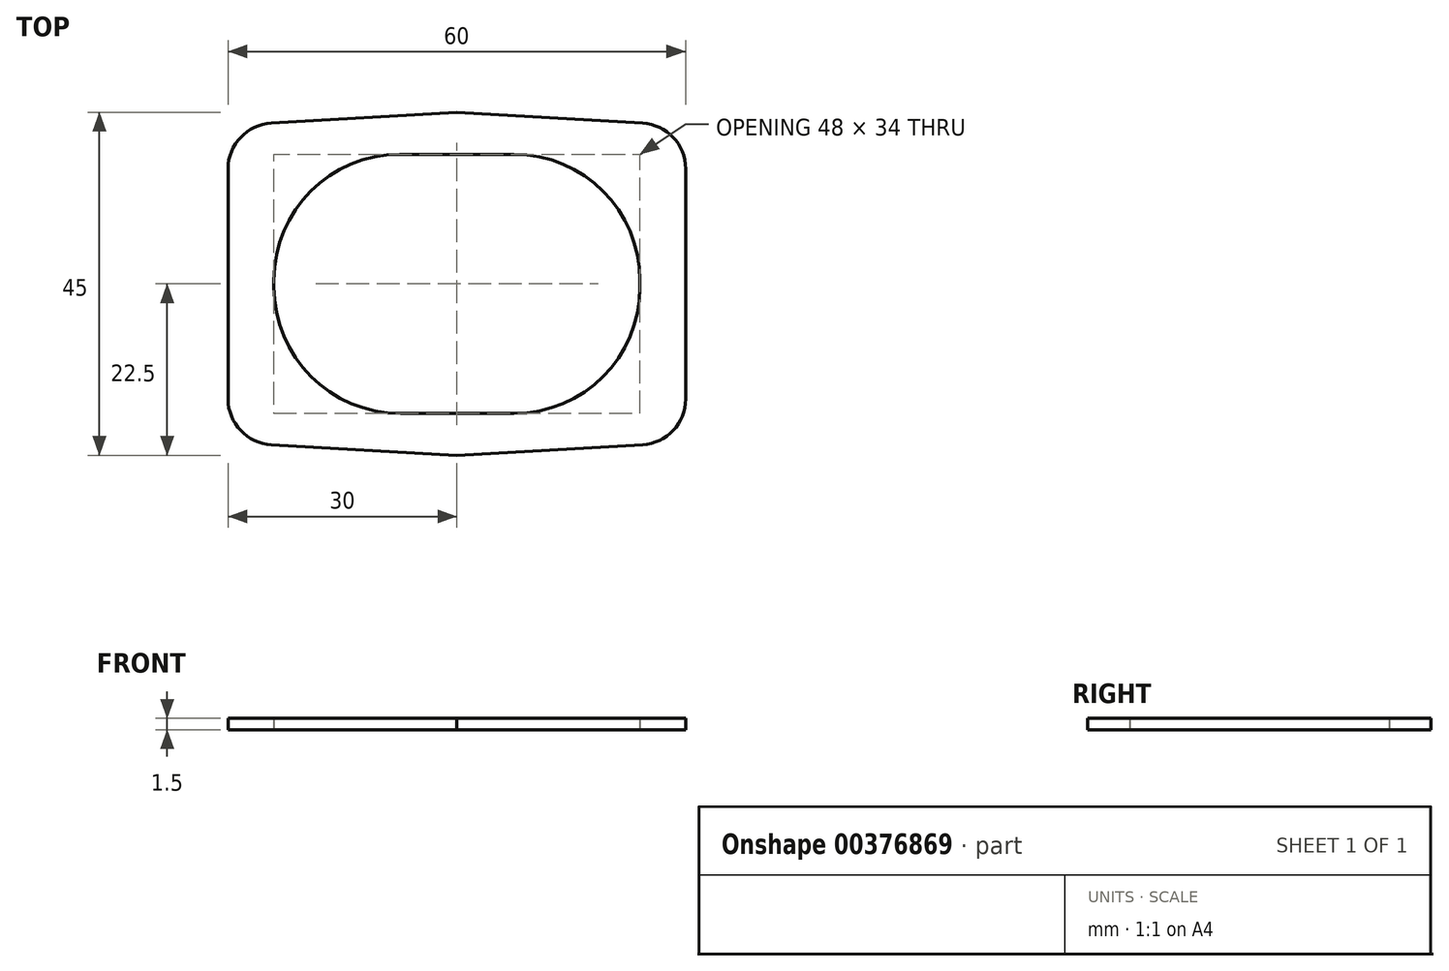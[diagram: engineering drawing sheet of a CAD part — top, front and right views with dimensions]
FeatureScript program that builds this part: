
annotation { "Feature Type Name" : "Feature", "Feature Type Description" : "" }
export const myFeature = defineFeature(function(context is Context, id is Id, definition is map)
    precondition{}
    {
        {
            var Q0;
            Q0=qCreatedBy(makeId("Top.planeOp"),FACE);
            var sketch = newSketch(context, id + "F0", { "sketchPlane" : qUnion([Q0])});
            skLineSegment(sketch, "E0.bottom", {"start": v(7.5, -17) * mm, "end": v(-7.4, -17) * mm});
            skLineSegment(sketch, "E0.top", {"start": v(7.5, 17) * mm, "end": v(-7.5, 17) * mm});
            skLineSegment(sketch, "E0.left", {"start": v(24, -0.5) * mm, "end": v(24, 0.5) * mm});
            skLineSegment(sketch, "E0.right", {"start": v(-24, -0.4) * mm, "end": v(-24, 0.5) * mm});
            skPoint(sketch, "E0.middle", {"position": v(0, 0) * mm});
            skPoint(sketch, "E1.visualSharp", {"position": v(-24, 17) * mm});
            skArc(sketch, "E1.filletArc", {"start": v(-7.5, 17) * mm, "mid": v(-19.17, 12.17) * mm, "end": v(-24, 0.5) * mm});
            skPoint(sketch, "E2.visualSharp", {"position": v(24, 17) * mm});
            skArc(sketch, "E2.filletArc", {"start": v(24, 0.5) * mm, "mid": v(19.17, 12.17) * mm, "end": v(7.5, 17) * mm});
            skPoint(sketch, "E3.visualSharp", {"position": v(24, -17) * mm});
            skArc(sketch, "E3.filletArc", {"start": v(7.5, -17) * mm, "mid": v(19.17, -12.17) * mm, "end": v(24, -0.5) * mm});
            skPoint(sketch, "E4.visualSharp", {"position": v(-24, -17) * mm});
            skArc(sketch, "E4.filletArc", {"start": v(-24, -0.4) * mm, "mid": v(-19.14, -12.14) * mm, "end": v(-7.4, -17) * mm});
            skLineSegment(sketch, "E5.left", {"start": v(30, -15.1) * mm, "end": v(30, 15.1) * mm});
            skLineSegment(sketch, "E5.right", {"start": v(-30, -15.1) * mm, "end": v(-30, 15.1) * mm});
            skPoint(sketch, "E6.visualSharp", {"position": v(-30, 22.5) * mm});
            skPoint(sketch, "E7.visualSharp", {"position": v(30, 22.5) * mm});
            skPoint(sketch, "E8.visualSharp", {"position": v(30, -22.5) * mm});
            skPoint(sketch, "E9.visualSharp", {"position": v(-30, -22.5) * mm});
            skPoint(sketch, "E10", {"position": v(0, 22.5) * mm});
            skPoint(sketch, "E11", {"position": v(0, -22.5) * mm});
            skLineSegment(sketch, "E12", {"start": v(0, 22.5) * mm, "end": v(-24.35, 21.1) * mm});
            skLineSegment(sketch, "E13", {"start": v(0, 22.5) * mm, "end": v(24.35, 21.1) * mm});
            skLineSegment(sketch, "E14", {"start": v(0, -22.5) * mm, "end": v(24.35, -21.1) * mm});
            skLineSegment(sketch, "E15", {"start": v(0, -22.5) * mm, "end": v(-24.35, -21.1) * mm});
            skArc(sketch, "E16.filletArc", {"start": v(-24.35, 21.1) * mm, "mid": v(-28.36, 19.22) * mm, "end": v(-30, 15.1) * mm});
            skArc(sketch, "E17.filletArc", {"start": v(30, 15.1) * mm, "mid": v(28.36, 19.22) * mm, "end": v(24.35, 21.1) * mm});
            skArc(sketch, "E18.filletArc", {"start": v(24.35, -21.1) * mm, "mid": v(28.36, -19.22) * mm, "end": v(30, -15.1) * mm});
            skArc(sketch, "E19.filletArc", {"start": v(-30, -15.1) * mm, "mid": v(-28.36, -19.22) * mm, "end": v(-24.35, -21.1) * mm});
            skSolve(sketch);
        }
        {
            var Q0;
            Q0=makeQuery(id+"F0.imprint","IMPRINT",FACE,{"disambiguationData":[TD([[makeQuery(id+"F0.imprint","IMPRINT",EDGE,{"derivedFrom":sQuery(id+"F0.wireOp",EDGE,"E0.bottom")}),1.0]])]});
            extrude(context, id + "F1", {"entities" : qUnion([Q0]), "depth" : 1.5 * mm});
        }
    });
